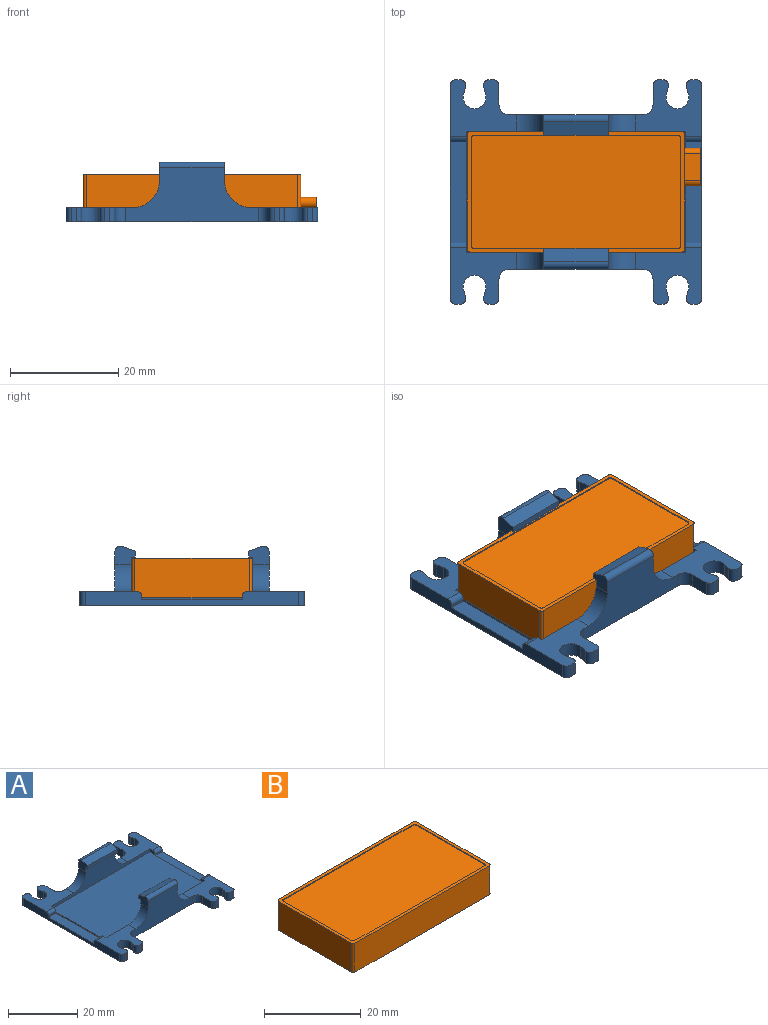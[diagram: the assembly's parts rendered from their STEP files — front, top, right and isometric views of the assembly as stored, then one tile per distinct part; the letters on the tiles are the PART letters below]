
ASSEMBLY  parts=2 mates=1
PART A: 88 faces, bbox 46.5x41.5x11 mm
  f0: plane 12.25x10.5mm, normal (0,0,1), area 79.5mm2, adj f4,f8,f27,f28,f29,f30,f31,f32
  f1: plane 12.25x10.5mm, normal (0,0,1), area 79.5mm2, adj f3,f5,f9,f10,f11,f12,f13,f14
  f2: plane 2x1.1mm, normal (-1,0,0), area 2mm2, adj f6,f9,f59,f82,f84
  f3: plane 2x1.1mm, normal (1,0,0), area 2mm2, adj f1,f9,f59,f78,f87
  f4: plane 39.5x2.6mm, normal (1,0,0), area 74.5mm2, adj f0,f6,f26,f27,f58,f81,f82,f83
  f5: plane 39.5x2.6mm, normal (-1,0,0), area 74.5mm2, adj f1,f7,f49,f50,f58,f77,f78,f79
  f6: plane 12.25x10.5mm, normal (0,0,1), area 79.5mm2, adj f2,f4,f9,f15,f16,f17,f18,f19
  f7: plane 12.25x10.5mm, normal (0,0,1), area 79.5mm2, adj f5,f38,f39,f40,f41,f42,f43,f44
  f8: plane 2x1.1mm, normal (-1,0,0), area 2mm2, adj f0,f56,f59,f81,f85
  f9: plane 40.5x7.5mm, normal (0,1,0), area 132.1mm2, adj f1,f2,f3,f6,f59,f62,f63,f64
  f10: cylinder r=1mm len=2.6mm, axis (0,0,-1), area 4.7mm2, adj f1,f11,f57,f58
  f11: plane 2.6x0.85mm, normal (0,-1,0), area 2.2mm2, adj f1,f10,f12,f58
  f12: cylinder r=1mm len=2.6mm, axis (0,0,-1), area 4.1mm2, adj f1,f11,f13,f58
  f13: plane 3.5x2.6mm, normal (1,0,0), area 9.1mm2, adj f1,f12,f14,f58
  f14: cylinder r=2mm len=2.6mm, axis (0,0,-1), area 8.2mm2, adj f1,f13,f15,f58
  f15: plane 24.5x9.98mm, normal (0,-1,0), area 163mm2, adj f1,f6,f14,f16,f58,f62,f63,f64
  f16: cylinder r=2mm len=2.6mm, axis (0,0,-1), area 8.2mm2, adj f6,f15,f17,f58
  f17: plane 3.5x2.6mm, normal (-1,0,0), area 9.1mm2, adj f6,f16,f18,f58
  f18: cylinder r=1mm len=2.6mm, axis (0,0,-1), area 4.1mm2, adj f6,f17,f19,f58
  f19: plane 2.6x0.85mm, normal (0,-1,0), area 2.2mm2, adj f6,f18,f20,f58
  f20: cylinder r=1mm len=2.6mm, axis (0,0,-1), area 4.7mm2, adj f6,f19,f21,f58
  f21: plane 2.6x1.53mm, normal (0.97,0.23,0), area 4.1mm2, adj f6,f20,f22,f58
  f22: cylinder r=2.1mm len=4.2mm, axis (0,0,-1), area 19.7mm2, adj f6,f21,f23,f58
  f23: plane 2.6x1.53mm, normal (-0.97,0.23,0), area 4.1mm2, adj f6,f22,f24,f58
  f24: cylinder r=1mm len=2.6mm, axis (0,0,-1), area 4.7mm2, adj f6,f23,f25,f58
  f25: plane 2.6x0.85mm, normal (0,-1,0), area 2.2mm2, adj f6,f24,f26,f58
  f26: cylinder r=1mm len=2.6mm, axis (0,0,-1), area 4.1mm2, adj f4,f6,f25,f58
  f27: cylinder r=1mm len=2.6mm, axis (0,0,-1), area 4.1mm2, adj f0,f4,f28,f58
  f28: plane 2.6x0.85mm, normal (0,1,0), area 2.2mm2, adj f0,f27,f29,f58
  f29: cylinder r=1mm len=2.6mm, axis (0,0,-1), area 4.7mm2, adj f0,f28,f30,f58
  f30: plane 2.6x1.53mm, normal (-0.97,-0.23,0), area 4.1mm2, adj f0,f29,f31,f58
  f31: cylinder r=2.1mm len=4.2mm, axis (0,0,-1), area 19.7mm2, adj f0,f30,f32,f58
  f32: plane 2.6x1.53mm, normal (0.97,-0.23,0), area 4.1mm2, adj f0,f31,f33,f58
  f33: cylinder r=1mm len=2.6mm, axis (0,0,-1), area 4.7mm2, adj f0,f32,f34,f58
  f34: plane 2.6x0.85mm, normal (0,1,0), area 2.2mm2, adj f0,f33,f35,f58
  f35: cylinder r=1mm len=2.6mm, axis (0,0,-1), area 4.1mm2, adj f0,f34,f36,f58
  f36: plane 3.5x2.6mm, normal (-1,0,0), area 9.1mm2, adj f0,f35,f37,f58
  f37: cylinder r=2mm len=2.6mm, axis (0,0,-1), area 8.2mm2, adj f0,f36,f38,f58
  f38: plane 24.5x9.98mm, normal (0,1,0), area 163mm2, adj f0,f7,f37,f39,f58,f60,f61,f66
  f39: cylinder r=2mm len=2.6mm, axis (0,0,-1), area 8.2mm2, adj f7,f38,f40,f58
  f40: plane 3.5x2.6mm, normal (1,0,0), area 9.1mm2, adj f7,f39,f41,f58
  f41: cylinder r=1mm len=2.6mm, axis (0,0,-1), area 4.1mm2, adj f7,f40,f42,f58
  f42: plane 2.6x0.85mm, normal (0,1,0), area 2.2mm2, adj f7,f41,f43,f58
  f43: cylinder r=1mm len=2.6mm, axis (0,0,-1), area 4.7mm2, adj f7,f42,f44,f58
  f44: plane 2.6x1.53mm, normal (-0.97,-0.23,0), area 4.1mm2, adj f7,f43,f45,f58
  f45: cylinder r=2.1mm len=4.2mm, axis (0,0,-1), area 19.7mm2, adj f7,f44,f46,f58
  f46: plane 2.6x1.53mm, normal (0.97,-0.23,0), area 4.1mm2, adj f7,f45,f47,f58
  f47: cylinder r=1mm len=2.6mm, axis (0,0,-1), area 4.7mm2, adj f7,f46,f48,f58
  f48: plane 2.6x0.85mm, normal (0,1,0), area 2.2mm2, adj f7,f47,f49,f58
  f49: cylinder r=1mm len=2.6mm, axis (0,0,-1), area 4.1mm2, adj f5,f7,f48,f58
  f50: cylinder r=1mm len=2.6mm, axis (0,0,-1), area 4.1mm2, adj f1,f5,f51,f58
  f51: plane 2.6x0.85mm, normal (0,-1,0), area 2.2mm2, adj f1,f50,f52,f58
  f52: cylinder r=1mm len=2.6mm, axis (0,0,-1), area 4.7mm2, adj f1,f51,f53,f58
  f53: plane 2.6x1.53mm, normal (0.97,0.23,0), area 4.1mm2, adj f1,f52,f54,f58
  f54: cylinder r=2.1mm len=4.2mm, axis (0,0,-1), area 19.7mm2, adj f1,f53,f57,f58
  f55: plane 2x1.1mm, normal (1,0,0), area 2mm2, adj f7,f56,f59,f77,f86
  f56: plane 40.5x7.5mm, normal (0,-1,0), area 132.1mm2, adj f0,f7,f8,f55,f59,f60,f61,f66
  f57: plane 2.6x1.53mm, normal (-0.97,0.23,0), area 4.1mm2, adj f1,f10,f54,f58
  f58: plane 46.5x41.5mm, normal (0,0,-1), area 1484.4mm2, adj f4,f5,f10,f11,f12,f13,f14,f15
  f59: plane 40.5x22.5mm, normal (0,0,1), area 911.2mm2, adj f2,f3,f8,f9,f55,f56,f76,f80
  f60: plane 3.8x3.38mm, normal (-1,0,0), area 10.3mm2, adj f38,f56,f67,f70,f71,f72,f75
  f61: plane 3.8x3.38mm, normal (1,0,0), area 10.3mm2, adj f38,f56,f66,f70,f71,f72,f75
  f62: plane 3.8x3.38mm, normal (-1,0,0), area 10.3mm2, adj f9,f15,f64,f68,f69,f73,f74
  f63: plane 3.8x3.38mm, normal (1,0,0), area 10.3mm2, adj f9,f15,f65,f68,f69,f73,f74
  f64: cylinder r=5mm len=5mm, axis (0,-1,0), area 23.6mm2, adj f1,f9,f15,f62
  f65: cylinder r=5mm len=5mm, axis (0,1,0), area 23.6mm2, adj f6,f9,f15,f63
  f66: cylinder r=5mm len=5mm, axis (0,1,0), area 23.6mm2, adj f0,f38,f56,f61
  f67: cylinder r=5mm len=5mm, axis (0,-1,0), area 23.6mm2, adj f7,f38,f56,f60
  f68: plane 12x1.1mm, normal (0,1,0), area 13.2mm2, adj f62,f63,f69,f73
  f69: plane 12x0.8mm, normal (0,0,-1), area 9.6mm2, adj f9,f62,f63,f68
  f70: plane 12x1.1mm, normal (0,-1,0), area 13.2mm2, adj f60,f61,f71,f72
  f71: plane 12x0.8mm, normal (0,0,-1), area 9.6mm2, adj f56,f60,f61,f70
  f72: plane 12x2.48mm, normal (0,-0.32,0.95), area 31.4mm2, adj f60,f61,f70,f75
  f73: plane 12x2.48mm, normal (0,0.32,0.95), area 31.4mm2, adj f62,f63,f68,f74
  f74: cylinder r=1mm len=12mm, axis (1,0,0), area 22.7mm2, adj f15,f62,f63,f73
  f75: cylinder r=1mm len=12mm, axis (1,0,0), area 22.7mm2, adj f38,f60,f61,f72
  f76: plane 18.5x0.4mm, normal (-1,0,0), area 7.4mm2, adj f59,f77,f78,f79
  f77: plane 3x0.5mm, normal (0,-1,0), area 1.5mm2, adj f5,f55,f76,f79,f86
  f78: plane 3x0.5mm, normal (0,1,0), area 1.5mm2, adj f3,f5,f76,f79,f87
  f79: plane 18.5x3mm, normal (0,0,1), area 55.5mm2, adj f5,f76,f77,f78
  f80: plane 18.5x0.4mm, normal (1,0,0), area 7.4mm2, adj f59,f81,f82,f83
  f81: plane 3x0.5mm, normal (0,-1,0), area 1.5mm2, adj f4,f8,f80,f83,f85
  f82: plane 3x0.5mm, normal (0,1,0), area 1.5mm2, adj f2,f4,f80,f83,f84
  f83: plane 18.5x3mm, normal (0,0,1), area 55.5mm2, adj f4,f80,f81,f82
  f84: cylinder r=1mm len=3mm, axis (-1,0,0), area 4.7mm2, adj f2,f4,f6,f82
  f85: cylinder r=1mm len=3mm, axis (1,0,0), area 4.7mm2, adj f0,f4,f8,f81
  f86: cylinder r=1mm len=3mm, axis (1,0,0), area 4.7mm2, adj f5,f7,f55,f77
  f87: cylinder r=1mm len=3mm, axis (-1,0,0), area 4.7mm2, adj f1,f3,f5,f78
PART B: 24 faces, bbox 43.2x22.3x7.3 mm
  f0: plane 21.25x7.3mm, normal (1,0,0), area 142mm2, adj f2,f3,f8,f9,f19,f20,f21,f22
  f1: plane 39.2x7.3mm, normal (0,-1,0), area 286.2mm2, adj f2,f7,f8,f9
  f2: cylinder r=0.5mm len=7.3mm, axis (0,0,-1), area 5.7mm2, adj f0,f1,f8,f9
  f3: cylinder r=0.5mm len=7.3mm, axis (0,0,-1), area 5.7mm2, adj f0,f4,f8,f9
  f4: plane 39.2x7.3mm, normal (0,1,0), area 286.2mm2, adj f3,f5,f8,f9
  f5: cylinder r=0.5mm len=7.3mm, axis (0,0,-1), area 5.7mm2, adj f4,f6,f8,f9
  f6: plane 21.25x7.3mm, normal (-1,0,0), area 155.1mm2, adj f5,f7,f8,f9
  f7: cylinder r=0.5mm len=7.3mm, axis (0,0,-1), area 5.7mm2, adj f1,f6,f8,f9
  f8: plane 40.2x22.25mm, normal (0,0,1), area 85.5mm2, adj f0,f1,f2,f3,f4,f5,f6,f7
  f9: plane 40.2x22.25mm, normal (0,0,-1), area 894.2mm2, adj f0,f1,f2,f3,f4,f5,f6,f7
  f10: plane 19.85x0.2mm, normal (1,0,0), area 4mm2, adj f8,f11,f17,f18
  f11: cylinder r=0.5mm len=0.5mm, axis (0,0,1), area 0.2mm2, adj f8,f10,f12,f18
  f12: plane 37.8x0.2mm, normal (0,1,0), area 7.6mm2, adj f8,f11,f13,f18
  f13: cylinder r=0.5mm len=0.5mm, axis (0,0,1), area 0.2mm2, adj f8,f12,f14,f18
  f14: plane 19.85x0.2mm, normal (-1,0,0), area 4mm2, adj f8,f13,f15,f18
  f15: cylinder r=0.5mm len=0.5mm, axis (0,0,1), area 0.2mm2, adj f8,f14,f16,f18
  f16: plane 37.8x0.2mm, normal (0,-1,0), area 7.6mm2, adj f8,f15,f17,f18
  f17: cylinder r=0.5mm len=0.5mm, axis (0,0,1), area 0.2mm2, adj f8,f10,f16,f18
  f18: plane 38.8x20.85mm, normal (0,0,1), area 808.8mm2, adj f10,f11,f12,f13,f14,f15,f16,f17
  f19: plane 5x3mm, normal (0,0,1), area 15mm2, adj f0,f20,f22,f23
  f20: cylinder r=1mm len=3mm, axis (-1,0,0), area 9.4mm2, adj f0,f19,f21,f23
  f21: plane 5x3mm, normal (0,0,-1), area 15mm2, adj f0,f20,f22,f23
  f22: cylinder r=1mm len=3mm, axis (-1,0,0), area 9.4mm2, adj f0,f19,f21,f23
  f23: plane 7x2mm, normal (1,0,0), area 13.1mm2, adj f19,f20,f21,f22
PLACE A at identity
PLACE B t=(0,0,1.5)mm
MATE planar B.f9 <-> A.f59  axis (0,0,-1) through (0,0,1.5)mm
